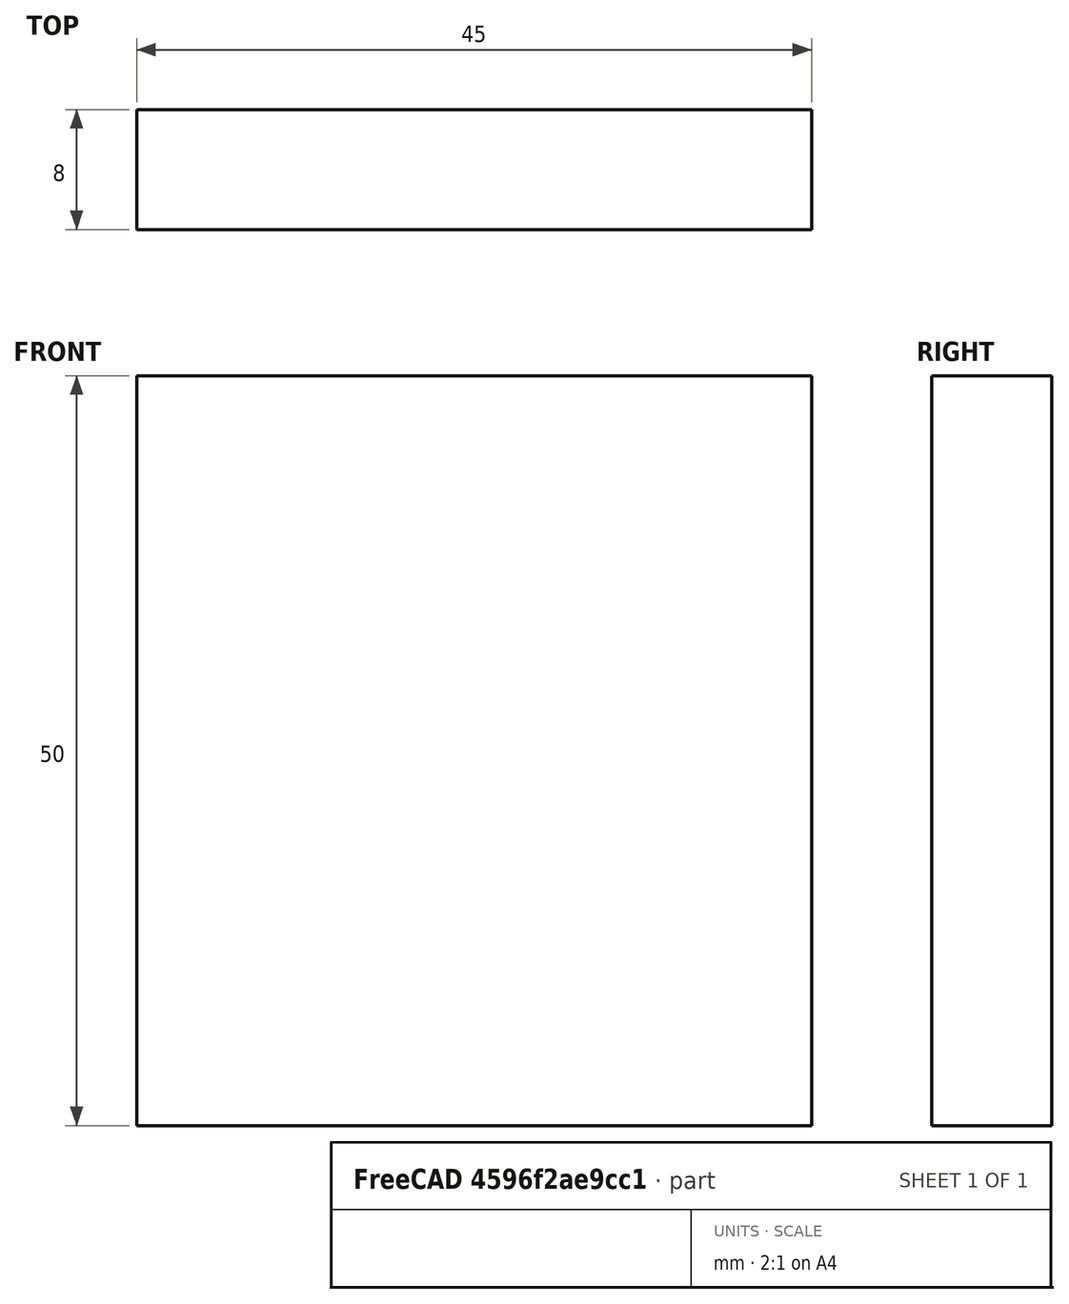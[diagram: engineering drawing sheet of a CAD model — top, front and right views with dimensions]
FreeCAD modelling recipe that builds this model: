
FCSTD DOCUMENT  (FreeCAD 0.15R4671 (Git))
Label: Flat Bar 45x8 EN10058 S235JR
License: All rights reserved
LicenseURL: http://en.wikipedia.org/wiki/All_rights_reserved
objects: Sketcher::SketchObject×1, Part::Extrusion×1
note: 2 computed .brp shape members not serialized (recipe doc carries the construction recipe); baked Part::Feature solids carry a one-line shape summary decoded from their .brp

FEATURE [Sketcher::SketchObject] Sketch
  sketch-geometry (4):
    g0: LineSegment StartX=-22.5 StartY=-4 StartZ=0 EndX=22.5 EndY=-4 EndZ=0
    g1: LineSegment StartX=22.5 StartY=-4 StartZ=0 EndX=22.5 EndY=4 EndZ=0
    g2: LineSegment StartX=22.5 StartY=4 StartZ=0 EndX=-22.5 EndY=4 EndZ=0
    g3: LineSegment StartX=-22.5 StartY=4 StartZ=0 EndX=-22.5 EndY=-4 EndZ=0
  constraints (12):
    c: Coincident(g0,g1)
    c: Coincident(g1,g2)
    c: Coincident(g2,g3)
    c: Coincident(g3,g0)
    c: Horizontal(g0)
    c: Horizontal(g2)
    c: Vertical(g1)
    c: Vertical(g3)
    c: Symmetric(g1,g2,g-2)
    c: Symmetric(g0,g1,g-1)
    c: DistanceY(g1) = 8
    c: DistanceX(g0) = 45
FEATURE [Part::Extrusion] Extrude  label="Flat Bar 45x8 EN10058 S235JR"
  Base = -> Sketch
  Dir = (0,0,50)
  Solid = true
